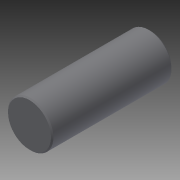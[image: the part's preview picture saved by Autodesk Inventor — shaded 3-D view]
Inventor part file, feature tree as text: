
AUTODESK INVENTOR PART (.ipt)
format: ipt  version: 2014 (Build 180170000, 170)  size: 110,592 bytes
history: native  units: in
note: dims shown in document units (in); Inventor stores cm internally (conversion verified against a paired STEP export)
features: other x35, revolve x1, sketch x1
ambient origin geometry x8: Origin, YZ Plane, XZ Plane, XY Plane, X Axis, Y Axis, Z Axis, Center Point
bodies: Solid1 (feature_tree)
feature tree (37):
  revolve  "Revolution1"  [1 undecoded]
  other  "dia1_XY"
  other  "dia1_YZ"
  other  "dia1_ZX"
  other  "dia1_X"
  other  "dia1_Y"
  other  "dia1_Z"
  other  "dia1_Center"
  other  "dia2_XY"
  other  "dia2_YZ"
  other  "dia2_ZX"
  other  "dia2_X"
  other  "dia2_Y"
  other  "dia2_Z"
  other  "dia2_Center"
  other  "pin_XY"
  other  "pin_YZ"
  other  "pin_ZX"
  other  "pin_X"
  other  "pin_Y"
  other  "pin_Z"
  other  "pin_Center"
  other  "pin1_XY"
  other  "pin1_YZ"
  other  "pin1_ZX"
  other  "pin1_X"
  other  "pin1_Y"
  other  "pin1_Z"
  other  "pin1_Center"
  other  "pin2_XY"
  other  "pin2_YZ"
  other  "pin2_ZX"
  other  "pin2_X"
  other  "pin2_Y"
  other  "pin2_Z"
  other  "pin2_Center"
  sketch  "Sketch_1"  dims[d0=360.0deg]
note: 1 required parameter value undecoded (feature->parameter linkage not recoverable at this tier; creation-order binding heuristic only, values carry confidence <= 0.55)
